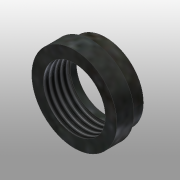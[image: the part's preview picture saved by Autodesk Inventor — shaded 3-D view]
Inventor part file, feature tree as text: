
AUTODESK INVENTOR PART (.ipt)
format: ipt  version: 2015 (Build 190159000, 159)  size: 115,712 bytes
history: native  units: mm
features: other x3, sketch x3
ambient origin geometry x8: Origin, YZ Plane, XZ Plane, XY Plane, X Axis, Y Axis, Z Axis, Center Point
bodies: Solid1 (feature_tree)
feature tree (6):
  other  "500-102.ipt"
  other  "Solid1::500-102.ipt"
  other  "TaggingFeature1"
  sketch  "Sketch1"  dims[d0=10.0mm]
  sketch  "Sketch2"
  sketch  "Sketch3"
